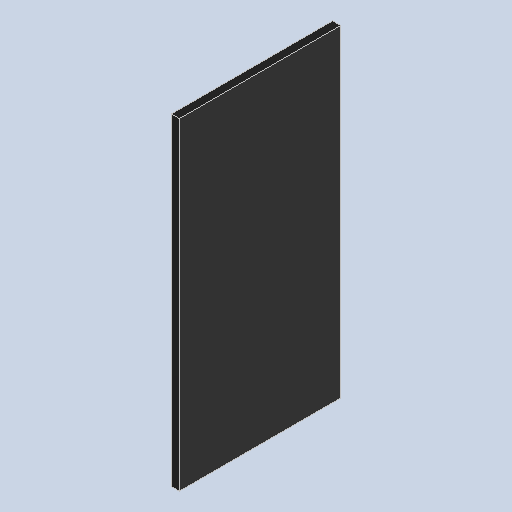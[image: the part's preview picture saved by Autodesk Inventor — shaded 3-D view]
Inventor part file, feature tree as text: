
AUTODESK INVENTOR PART (.ipt)
format: ipt  version: 2025 (Build 290162010, 162A)  size: 122,880 bytes
history: native  units: mm
features: extrude x1, sketch x1
ambient origin geometry x8: Origin, YZ Plane, XZ Plane, XY Plane, X Axis, Y Axis, Z Axis, Center Point
bodies: Volumenkörper1 (feature_tree)
feature tree (2):
  extrude  "Extrusion1"  Depth=40.0mm
  sketch  "Skizze1"  dims[d0=20.0mm d1=40.0mm d2=1.0mm d3=0.0mm]
